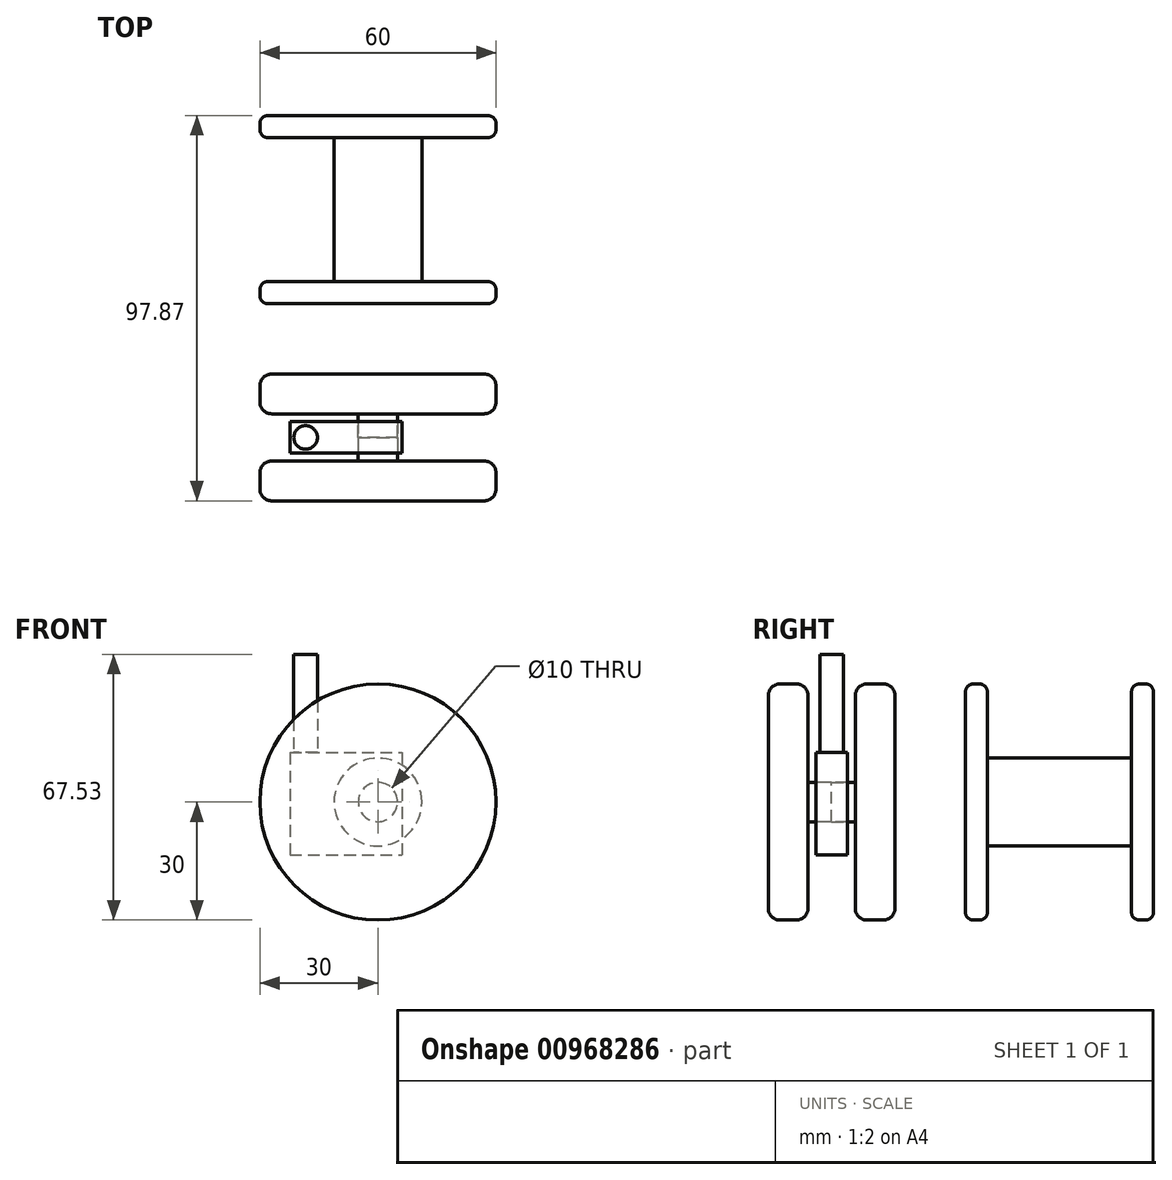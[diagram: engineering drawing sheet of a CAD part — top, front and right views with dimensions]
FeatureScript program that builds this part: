
annotation { "Feature Type Name" : "Feature", "Feature Type Description" : "" }
export const myFeature = defineFeature(function(context is Context, id is Id, definition is map)
    precondition{}
    {
        {
            var Q0;
            Q0=qCreatedBy(makeId("Front.planeOp"),FACE);
            var sketch = newSketch(context, id + "F0", { "sketchPlane" : qUnion([Q0])});
            skCircle(sketch, "E0", {"center": v(0, 0) * mm, "radius": 30 * mm});
            skSolve(sketch);
        }
        {
            var Q0;
            Q0=makeQuery(id+"F0.imprint","IMPRINT",FACE,{"disambiguationData":[TD([[makeQuery(id+"F0.imprint","IMPRINT",EDGE,{"derivedFrom":sQuery(id+"F0.wireOp",EDGE,"E0")}),1.0]])]});
            extrude(context, id + "F1", {"entities" : qUnion([Q0]), "oppositeDirection" : true, "depth" : 10.1 * mm, "offsetDistance" : 25 * mm});
        }
        {
            var Q0;
            Q0=makeQuery(id+"F1.opExtrude","CAP_EDGE",EDGE,{"disambiguationData":[OSD([sQuery(id+"F0.wireOp",EDGE,"E0")])],"isStart":false});
            var Q1;
            Q1=makeQuery(id+"F1.opExtrude","CAP_EDGE",EDGE,{"disambiguationData":[OSD([sQuery(id+"F0.wireOp",EDGE,"E0")])],"isStart":true});
            fillet(context, id + "F2", {"entities" : qUnion([Q0, Q1]), "radius" : 3 * mm, "tangentPropagation" : true, "allowEdgeOverflow" : false});
        }
        {
            var Q0;
            Q0=makeQuery(id+"F1.opExtrude","CAP_FACE",FACE,{"disambiguationData":[OSD([sQuery(id+"F0.wireOp",EDGE,"E0")])],"isStart":true});
            var sketch = newSketch(context, id + "F3", { "sketchPlane" : qUnion([Q0])});
            skCircle(sketch, "E1", {"center": v(0, 0) * mm, "radius": 5 * mm});
            skSolve(sketch);
        }
        {
            var Q0;
            Q0=makeQuery(id+"F3.imprint","IMPRINT",FACE,{"disambiguationData":[TD([[makeQuery(id+"F3.imprint","IMPRINT",EDGE,{"derivedFrom":sQuery(id+"F3.wireOp",EDGE,"E1")}),1.0]])]});
            var Q1;
            Q1=sQuery(id+"F3.wireOp",EDGE,"E1");
            extrude(context, id + "F4", {"entities" : qUnion([Q0]), "operationType" : NewBodyOperationType.ADD, "surfaceEntities" : qUnion([Q1]), "depth" : 6 * mm, "offsetDistance" : 25 * mm});
        }
        {
            var Q0;
            Q0=makeQuery(id+"F1.opExtrude","SWEPT_BODY",BODY,{"disambiguationData":[OSD([sQuery(id+"F0.wireOp",EDGE,"E0")])]});
            var Q1;
            Q1=makeQuery(id+"F4.opExtrude","CAP_FACE",FACE,{"disambiguationData":[OSD([sQuery(id+"F3.wireOp",EDGE,"E1")])],"isStart":false});
            mirror(context, id + "F5", {"entities" : qUnion([Q0]), "mirrorPlane" : qUnion([Q1])});
        }
        {
            var Q0;
            Q0=makeQuery(id+"F4.opExtrude","CAP_FACE",FACE,{"disambiguationData":[OSD([sQuery(id+"F3.wireOp",EDGE,"E1")])],"isStart":false});
            var sketch = newSketch(context, id + "F6", { "sketchPlane" : qUnion([Q0])});
            skLineSegment(sketch, "E2.bottom", {"start": v(-22.38, 12.53) * mm, "end": v(6.17, 12.53) * mm});
            skLineSegment(sketch, "E2.top", {"start": v(-22.38, -13.4) * mm, "end": v(6.17, -13.4) * mm});
            skLineSegment(sketch, "E2.left", {"start": v(-22.38, 12.53) * mm, "end": v(-22.38, -13.4) * mm});
            skLineSegment(sketch, "E2.right", {"start": v(6.17, 12.53) * mm, "end": v(6.17, -13.4) * mm});
            skSolve(sketch);
        }
        {
            var Q0;
            Q0=makeQuery(id+"F6.imprint","IMPRINT",FACE,{"disambiguationData":[TD([[makeQuery(id+"F6.imprint","IMPRINT",EDGE,{"derivedFrom":sQuery(id+"F6.wireOp",EDGE,"E2.bottom")}),-1.0]])]});
            extrude(context, id + "F7", {"entities" : qUnion([Q0]), "endBound" : BoundingType.SYMMETRIC, "oppositeDirection" : true, "depth" : 8 * mm, "offsetDistance" : 25 * mm});
        }
        {
            var Q0;
            Q0=makeQuery(id+"F7.opExtrude","SWEPT_FACE",FACE,{"disambiguationData":[OSD([sQuery(id+"F6.wireOp",EDGE,"E2.bottom")])]});
            var sketch = newSketch(context, id + "F8", { "sketchPlane" : qUnion([Q0])});
            skLineSegment(sketch, "E3", {"start": v(-18.38, -10) * mm, "end": v(-18.38, -2) * mm, "construction": true});
            skCircle(sketch, "E4", {"center": v(-18.38, -6) * mm, "radius": 3 * mm});
            skSolve(sketch);
        }
        {
            var Q0;
            Q0=makeQuery(id+"F8.imprint","IMPRINT",FACE,{"disambiguationData":[TD([[makeQuery(id+"F8.imprint","IMPRINT",EDGE,{"derivedFrom":sQuery(id+"F8.wireOp",EDGE,"E4")}),1.0]])]});
            var Q1;
            Q1=sQuery(id+"F8.wireOp",EDGE,"E4");
            extrude(context, id + "F9", {"entities" : qUnion([Q0]), "operationType" : NewBodyOperationType.ADD, "surfaceEntities" : qUnion([Q1]), "depth" : 25 * mm, "offsetDistance" : 25 * mm});
        }
        {
            var Q0;
            Q0=qCreatedBy(makeId("Right.planeOp"),FACE);
            var sketch = newSketch(context, id + "F10", { "sketchPlane" : qUnion([Q0])});
            skLineSegment(sketch, "E5", {"start": v(51.88, 11.16) * mm, "end": v(33.58, 11.16) * mm});
            skLineSegment(sketch, "E6", {"start": v(33.58, 11.16) * mm, "end": v(33.58, 27.99) * mm});
            skLineSegment(sketch, "E7", {"start": v(31.58, 29.99) * mm, "end": v(29.99, 29.99) * mm});
            skLineSegment(sketch, "E8", {"start": v(27.99, 27.99) * mm, "end": v(27.99, 0) * mm});
            skLineSegment(sketch, "E9", {"start": v(27.99, 0) * mm, "end": v(51.88, 0) * mm});
            skLineSegment(sketch, "E10", {"start": v(51.88, 0) * mm, "end": v(51.88, 11.16) * mm});
            skPoint(sketch, "E11.visualSharp", {"position": v(33.58, 29.99) * mm});
            skArc(sketch, "E11.filletArc", {"start": v(33.58, 27.99) * mm, "mid": v(33, 29.4) * mm, "end": v(31.58, 29.99) * mm});
            skPoint(sketch, "E12.visualSharp", {"position": v(27.99, 29.99) * mm});
            skArc(sketch, "E12.filletArc", {"start": v(29.99, 29.99) * mm, "mid": v(28.57, 29.4) * mm, "end": v(27.99, 27.99) * mm});
            skLineSegment(sketch, "E13.MirrorCS", {"start": v(51.88, 11.16) * mm, "end": v(70.18, 11.16) * mm});
            skLineSegment(sketch, "E14.MirrorCS", {"start": v(75.77, 0) * mm, "end": v(51.88, 0) * mm});
            skLineSegment(sketch, "E15.MirrorCS", {"start": v(75.77, 27.99) * mm, "end": v(75.77, 0) * mm});
            skArc(sketch, "E16.MirrorCS", {"start": v(70.18, 27.99) * mm, "mid": v(70.76, 29.4) * mm, "end": v(72.18, 29.99) * mm});
            skLineSegment(sketch, "E17.MirrorCS", {"start": v(72.18, 29.99) * mm, "end": v(73.77, 29.99) * mm});
            skArc(sketch, "E18.MirrorCS", {"start": v(73.77, 29.99) * mm, "mid": v(75.18, 29.4) * mm, "end": v(75.77, 27.99) * mm});
            skLineSegment(sketch, "E19.MirrorCS", {"start": v(70.18, 11.16) * mm, "end": v(70.18, 27.99) * mm});
            skSolve(sketch);
        }
        {
            var Q0;
            Q0=makeQuery(id+"F10.imprint","IMPRINT",FACE,{"disambiguationData":[TD([[makeQuery(id+"F10.imprint","IMPRINT",EDGE,{"derivedFrom":sQuery(id+"F10.wireOp",EDGE,"E10")}),-1.0]])]});
            var Q1;
            Q1=makeQuery(id+"F10.imprint","IMPRINT",FACE,{"disambiguationData":[TD([[makeQuery(id+"F10.imprint","IMPRINT",EDGE,{"derivedFrom":sQuery(id+"F10.wireOp",EDGE,"E5")}),1.0]])]});
            var Q2;
            Q2=sQuery(id+"F10.wireOp",EDGE,"E14.MirrorCS");
            revolve(context, id + "F11", {"surfaceOperationType" : NewSurfaceOperationType.NEW, "entities" : qUnion([Q0, Q1]), "axis" : qUnion([Q2]), "revolveType" : RevolveType.FULL});
        }
        {
            var Q0;
            Q0=makeQuery(id+"F11.opRevolve","SWEPT_FACE",FACE,{"disambiguationData":[OSD([sQuery(id+"F10.wireOp",EDGE,"E15.MirrorCS")])]});
            var Q1;
            Q1=makeQuery(id+"F11.opRevolve","SWEPT_FACE",FACE,{"disambiguationData":[OSD([sQuery(id+"F10.wireOp",EDGE,"E8")])]});
            cPlane(context, id + "F12", {"entities" : qUnion([Q0, Q1]), "cplaneType" : CPlaneType.MID_PLANE, "offset" : 25 * mm, "width" : 150 * mm, "height" : 150 * mm});
        }
    });
